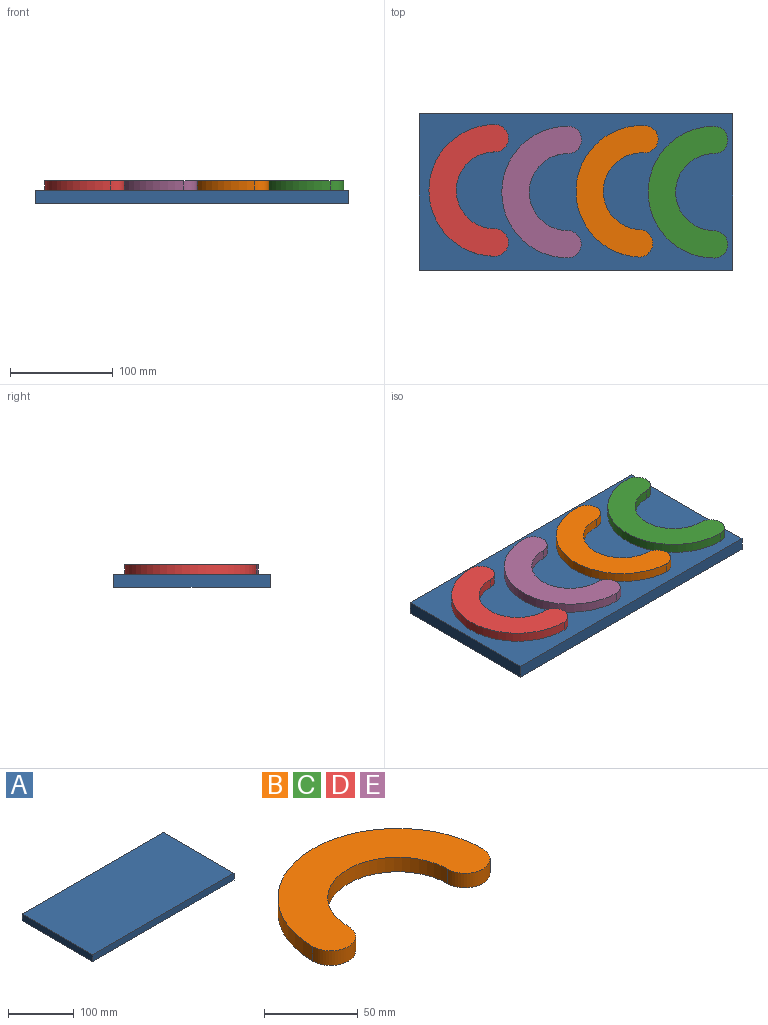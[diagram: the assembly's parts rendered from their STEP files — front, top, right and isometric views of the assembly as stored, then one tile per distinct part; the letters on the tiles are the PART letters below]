
ASSEMBLY  parts=5 mates=4
PART A: 6 faces, bbox 304.8x152.4x12.7 mm
  f0: plane 304.8x12.7mm, normal (0,1,0), area 3871mm2, adj f1,f3,f4,f5
  f1: plane 152.4x12.7mm, normal (-1,0,0), area 1935.5mm2, adj f0,f2,f4,f5
  f2: plane 304.8x12.7mm, normal (0,-1,0), area 3871mm2, adj f1,f3,f4,f5
  f3: plane 152.4x12.7mm, normal (1,0,0), area 1935.5mm2, adj f0,f2,f4,f5
  f4: plane 304.8x152.4mm, normal (0,0,1), area 46451.5mm2, adj f0,f1,f2,f3
  f5: plane 304.8x152.4mm, normal (0,0,-1), area 46451.5mm2, adj f0,f1,f2,f3
PART B: 6 faces, bbox 128.3x77.5x9.5 mm
  f0: cylinder r=37.46mm len=74.93mm, axis (0,0,-1), area 1121.1mm2, adj f1,f3,f4,f5
  f1: cylinder r=13.33mm len=26.67mm, axis (0,0,-1), area 399mm2, adj f0,f2,f4,f5
  f2: cylinder r=64.13mm len=128.27mm, axis (0,0,-1), area 1919.2mm2, adj f1,f3,f4,f5
  f3: cylinder r=13.33mm len=26.67mm, axis (0,0,-1), area 399mm2, adj f0,f2,f4,f5
  f4: plane 128.27x77.47mm, normal (0,0,1), area 4815mm2, adj f0,f1,f2,f3
  f5: plane 128.27x77.47mm, normal (0,0,-1), area 4815mm2, adj f0,f1,f2,f3
PART C: same geometry as B
PART D: same geometry as B
PART E: same geometry as B
PLACE A t=(-106.72,-134.06,-71.51)mm fixed
PLACE B rot(axis=(0,0,1),87.1deg) t=(109.76,-57.21,-58.81)mm
PLACE C rot(axis=(0,0,1),90deg) t=(180.09,-58.04,-58.81)mm
PLACE D rot(axis=(0,0,1),90deg) t=(-33.44,-56.33,-58.81)mm
PLACE E rot(axis=(0,0,1),89.7deg) t=(37.55,-57.94,-58.81)mm
MATE planar D.f5 <-> A.f4  axis (0,0,-1) through (-62.02,-56.33,-58.81)mm
MATE planar B.f5 <-> A.f4  axis (0,0,-1) through (81.21,-55.79,-58.81)mm
MATE planar E.f5 <-> A.f4  axis (0,0,-1) through (8.96,-57.81,-58.81)mm
MATE planar C.f3 <-> A.f4  axis (0,0,-1) through (180.09,-108.84,-58.81)mm
